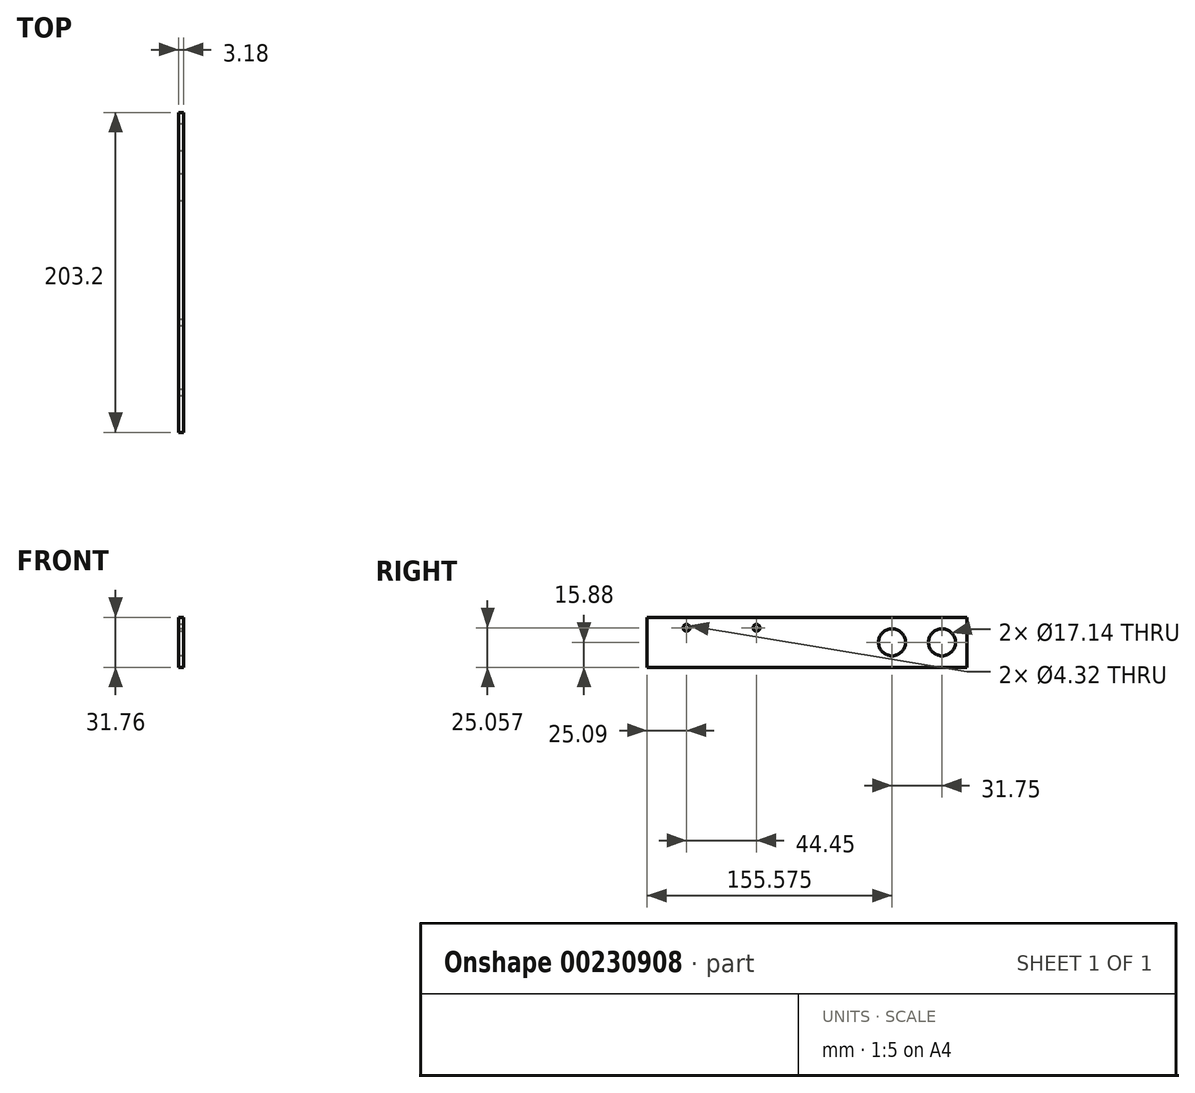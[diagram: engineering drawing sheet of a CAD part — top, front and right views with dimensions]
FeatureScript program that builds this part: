
annotation { "Feature Type Name" : "Feature", "Feature Type Description" : "" }
export const myFeature = defineFeature(function(context is Context, id is Id, definition is map)
    precondition{}
    {
        {
            var Q0;
            Q0=qCreatedBy(makeId("Right.planeOp"),FACE);
            var sketch = newSketch(context, id + "F0", { "sketchPlane" : qUnion([Q0])});
            skLineSegment(sketch, "E0.bottom", {"start": v(-101.6, -15.88) * mm, "end": v(101.6, -15.88) * mm});
            skLineSegment(sketch, "E0.top", {"start": v(-101.6, 15.88) * mm, "end": v(101.6, 15.88) * mm});
            skLineSegment(sketch, "E0.left", {"start": v(-101.6, -15.88) * mm, "end": v(-101.6, 15.87) * mm});
            skLineSegment(sketch, "E0.right", {"start": v(101.6, -15.88) * mm, "end": v(101.6, 15.87) * mm});
            skPoint(sketch, "E0.middle", {"position": v(0, 0) * mm});
            skSolve(sketch);
        }
        {
            var Q0;
            Q0 = qSketchRegion(id + "F0", true);
            extrude(context, id + "F1", {"entities" : qUnion([Q0]), "oppositeDirection" : true, "depth" : 3.17 * mm});
        }
        {
            var Q0;
            Q0=makeQuery(id+"F1.opExtrude","CAP_FACE",FACE,{"disambiguationData":[OSD([sQuery(id+"F0.wireOp",EDGE,"E0.bottom"),sQuery(id+"F0.wireOp",EDGE,"E0.top"),sQuery(id+"F0.wireOp",EDGE,"E0.left"),sQuery(id+"F0.wireOp",EDGE,"E0.right")])],"isStart":true});
            var sketch = newSketch(context, id + "F2", { "sketchPlane" : qUnion([Q0])});
            skLineSegment(sketch, "E1", {"start": v(-101.6, 0) * mm, "end": v(101.6, 0) * mm, "construction": true});
            skLineSegment(sketch, "E2", {"start": v(0, 15.88) * mm, "end": v(0, -15.88) * mm, "construction": true});
            skPoint(sketch, "E3", {"position": v(85.73, 0) * mm});
            skPoint(sketch, "E4", {"position": v(53.98, 0) * mm});
            skPoint(sketch, "E5", {"position": v(-32.06, 9.18) * mm});
            skPoint(sketch, "E6", {"position": v(-76.5, 9.18) * mm});
            skLineSegment(sketch, "E7", {"start": v(0, 9.18) * mm, "end": v(-101.6, 9.18) * mm, "construction": true});
            skSolve(sketch);
        }
        {
            var Q0;
            Q0=sQuery(id+"F2.wireOp",VERTEX,"E3");
            var Q1;
            Q1=sQuery(id+"F2.wireOp",VERTEX,"E4");
            var Q2;
            Q2=makeQuery(id+"F1.opExtrude","SWEPT_BODY",BODY,{"disambiguationData":[OSD([sQuery(id+"F0.wireOp",EDGE,"E0.bottom"),sQuery(id+"F0.wireOp",EDGE,"E0.top"),sQuery(id+"F0.wireOp",EDGE,"E0.left"),sQuery(id+"F0.wireOp",EDGE,"E0.right")])]});
            hole(context, id + "F3", {"style" : HoleStyle.SIMPLE, "endStyle" : HoleEndStyle.THROUGH, "holeDiameter" : 17.14 * mm, "locations" : qUnion([Q0, Q1]), "scope" : qUnion([Q2]), "isTappedThrough" : true});
        }
        {
            var Q0;
            Q0=sQuery(id+"F2.wireOp",VERTEX,"E6");
            var Q1;
            Q1=sQuery(id+"F2.wireOp",VERTEX,"E5");
            var Q2;
            Q2=makeQuery(id+"F1.opExtrude","SWEPT_BODY",BODY,{"disambiguationData":[OSD([sQuery(id+"F0.wireOp",EDGE,"E0.bottom"),sQuery(id+"F0.wireOp",EDGE,"E0.top"),sQuery(id+"F0.wireOp",EDGE,"E0.left"),sQuery(id+"F0.wireOp",EDGE,"E0.right")])]});
            hole(context, id + "F4", {"style" : HoleStyle.SIMPLE, "endStyle" : HoleEndStyle.THROUGH, "standardTappedOrClearance" : lookupTablePath({ "standard" : "ANSI", "fit" : "Close", "size" : "#8", "type" : "Clearance" }), "standardBlindInLast" : lookupTablePath({ "fit" : "Close", "standard" : "ANSI", "size" : "#8", "type" : "Clearance" }), "holeDiameter" : 4.32 * mm, "locations" : qUnion([Q0, Q1]), "scope" : qUnion([Q2]), "isTappedThrough" : true});
        }
    });
